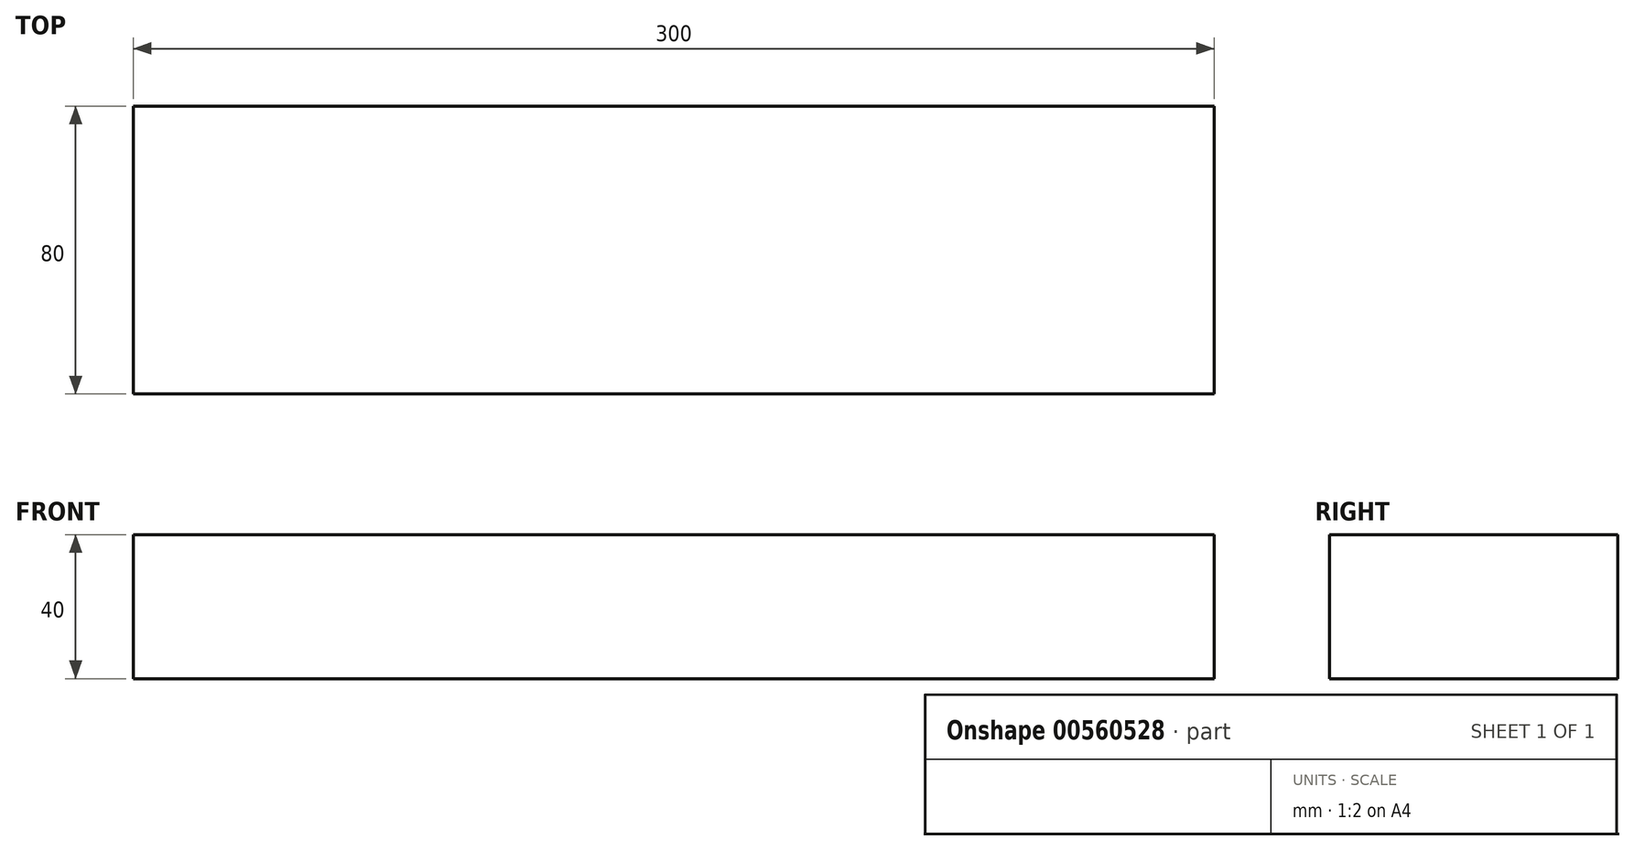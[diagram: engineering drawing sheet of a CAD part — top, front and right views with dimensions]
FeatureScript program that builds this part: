
annotation { "Feature Type Name" : "Feature", "Feature Type Description" : "" }
export const myFeature = defineFeature(function(context is Context, id is Id, definition is map)
    precondition{}
    {
        {
            var Q0;
            Q0=qCreatedBy(makeId("Top.planeOp"),FACE);
            var sketch = newSketch(context, id + "F0", { "sketchPlane" : qUnion([Q0])});
            skLineSegment(sketch, "E0.bottom", {"start": v(0, 0) * mm, "end": v(300, 0) * mm});
            skLineSegment(sketch, "E0.top", {"start": v(0, 80) * mm, "end": v(300, 80) * mm});
            skLineSegment(sketch, "E0.left", {"start": v(0, 0) * mm, "end": v(0, 80) * mm});
            skLineSegment(sketch, "E0.right", {"start": v(300, 0) * mm, "end": v(300, 80) * mm});
            skSolve(sketch);
        }
        {
            var Q0;
            Q0 = qSketchRegion(id + "F0", true);
            extrude(context, id + "F1", {"entities" : qUnion([Q0]), "depth" : 40 * mm, "offsetDistance" : 25 * mm});
        }
    });
